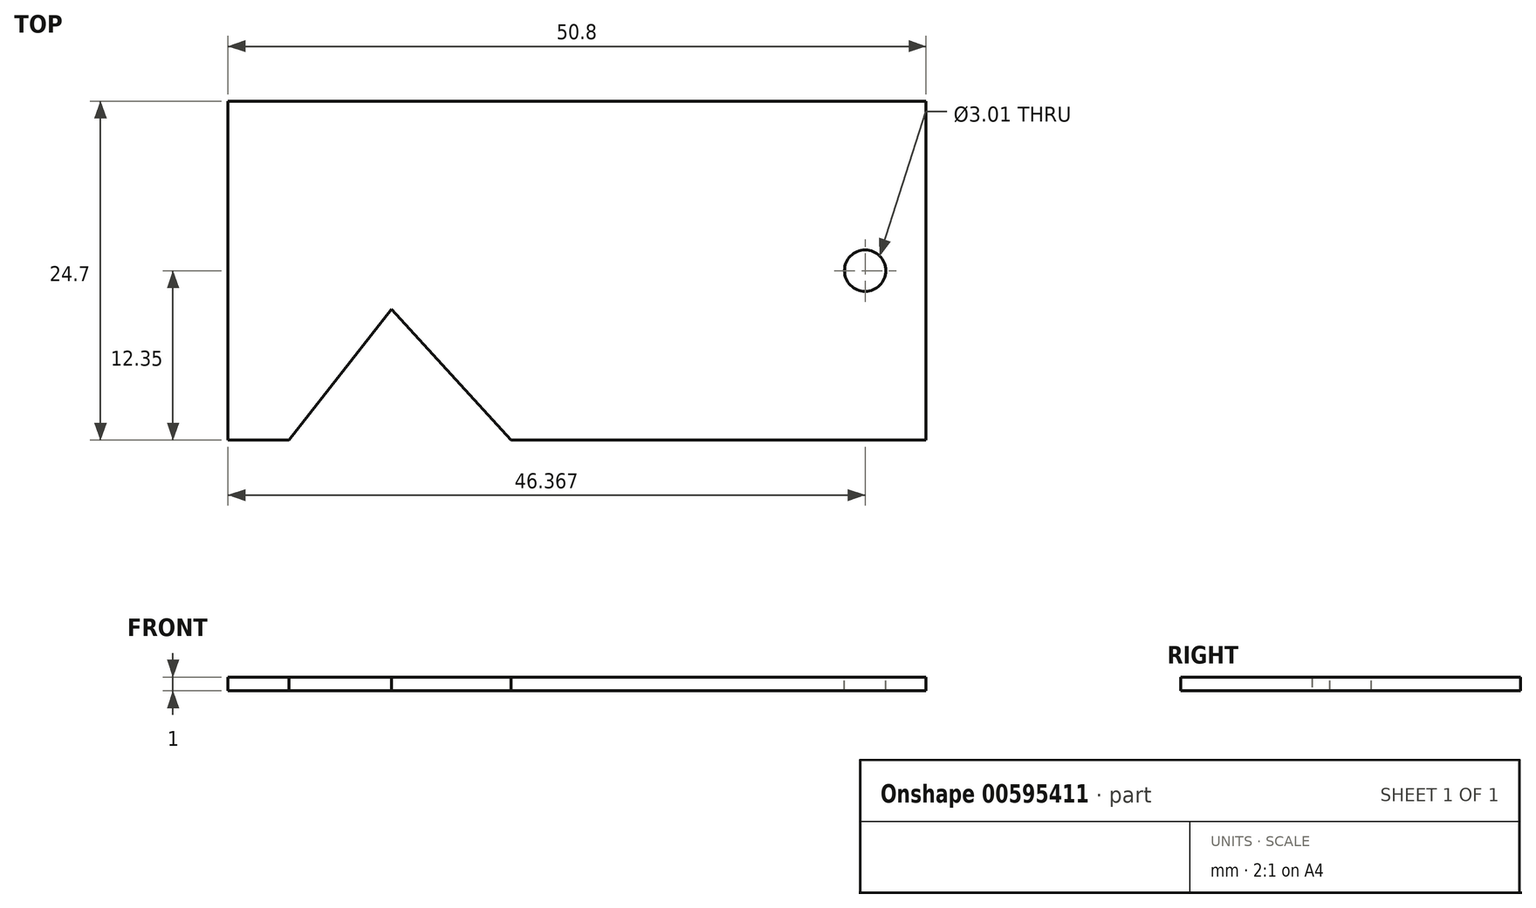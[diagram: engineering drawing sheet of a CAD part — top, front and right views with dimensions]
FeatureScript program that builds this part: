
annotation { "Feature Type Name" : "Feature", "Feature Type Description" : "" }
export const myFeature = defineFeature(function(context is Context, id is Id, definition is map)
    precondition{}
    {
        {
            var Q0;
            Q0=qCreatedBy(makeId("Top.planeOp"),FACE);
            var sketch = newSketch(context, id + "F0", { "sketchPlane" : qUnion([Q0])});
            skLineSegment(sketch, "E0.bottom", {"start": v(-25.4, 12.35) * mm, "end": v(25.4, 12.35) * mm});
            skLineSegment(sketch, "E0.top", {"start": v(-25.4, -12.35) * mm, "end": v(25.4, -12.35) * mm});
            skLineSegment(sketch, "E0.left", {"start": v(-25.4, 12.35) * mm, "end": v(-25.4, -12.35) * mm});
            skLineSegment(sketch, "E0.right", {"start": v(25.4, 12.35) * mm, "end": v(25.4, -12.35) * mm});
            skPoint(sketch, "E0.middle", {"position": v(0, 0) * mm});
            skSolve(sketch);
        }
        {
            var Q0;
            Q0 = qSketchRegion(id + "F0", true);
            extrude(context, id + "F1", {"entities" : qUnion([Q0]), "depth" : 1 * mm, "offsetDistance" : 25 * mm});
        }
        {
            var Q0;
            Q0=makeQuery(id+"F1.opExtrude","CAP_FACE",FACE,{"disambiguationData":[OSD([sQuery(id+"F0.wireOp",EDGE,"E0.bottom"),sQuery(id+"F0.wireOp",EDGE,"E0.top"),sQuery(id+"F0.wireOp",EDGE,"E0.left"),sQuery(id+"F0.wireOp",EDGE,"E0.right")])],"isStart":false});
            var sketch = newSketch(context, id + "F2", { "sketchPlane" : qUnion([Q0])});
            skCircle(sketch, "E1", {"center": v(20.97, 0) * mm, "radius": 1.5 * mm});
            skSolve(sketch);
        }
        {
            var Q0;
            Q0 = qSketchRegion(id + "F2", true);
            extrude(context, id + "F3", {"entities" : qUnion([Q0]), "operationType" : NewBodyOperationType.REMOVE, "oppositeDirection" : true, "depth" : 25 * mm, "offsetDistance" : 25 * mm});
        }
        {
            var Q0;
            Q0=makeQuery(id+"F1.opExtrude","CAP_FACE",FACE,{"disambiguationData":[OSD([sQuery(id+"F0.wireOp",EDGE,"E0.bottom"),sQuery(id+"F0.wireOp",EDGE,"E0.top"),sQuery(id+"F0.wireOp",EDGE,"E0.left"),sQuery(id+"F0.wireOp",EDGE,"E0.right")])],"isStart":true});
            var sketch = newSketch(context, id + "F4", { "sketchPlane" : qUnion([Q0])});
            skLineSegment(sketch, "E2", {"start": v(-20.96, 12.35) * mm, "end": v(-13.52, 2.81) * mm});
            skLineSegment(sketch, "E3", {"start": v(-4.8, 12.35) * mm, "end": v(-13.52, 2.81) * mm});
            skLineSegment(sketch, "E4", {"start": v(-4.8, 12.35) * mm, "end": v(4.04, 4.27) * mm});
            skLineSegment(sketch, "E5", {"start": v(5.53, 4.27) * mm, "end": v(12.91, 12.35) * mm});
            skLineSegment(sketch, "E6", {"start": v(12.91, 12.35) * mm, "end": v(3.08, 21.33) * mm});
            skLineSegment(sketch, "E7", {"start": v(3.08, 21.33) * mm, "end": v(-4.8, 12.35) * mm});
            skLineSegment(sketch, "E8", {"start": v(-4.8, 12.35) * mm, "end": v(-13.52, 21.33) * mm});
            skLineSegment(sketch, "E9", {"start": v(-13.52, 21.33) * mm, "end": v(-20.96, 12.35) * mm});
            skSolve(sketch);
        }
        {
            var Q0;
            Q0 = qSketchRegion(id + "F4", true);
            extrude(context, id + "F5", {"entities" : qUnion([Q0]), "operationType" : NewBodyOperationType.REMOVE, "oppositeDirection" : true, "depth" : 25 * mm, "offsetDistance" : 25 * mm});
        }
    });
